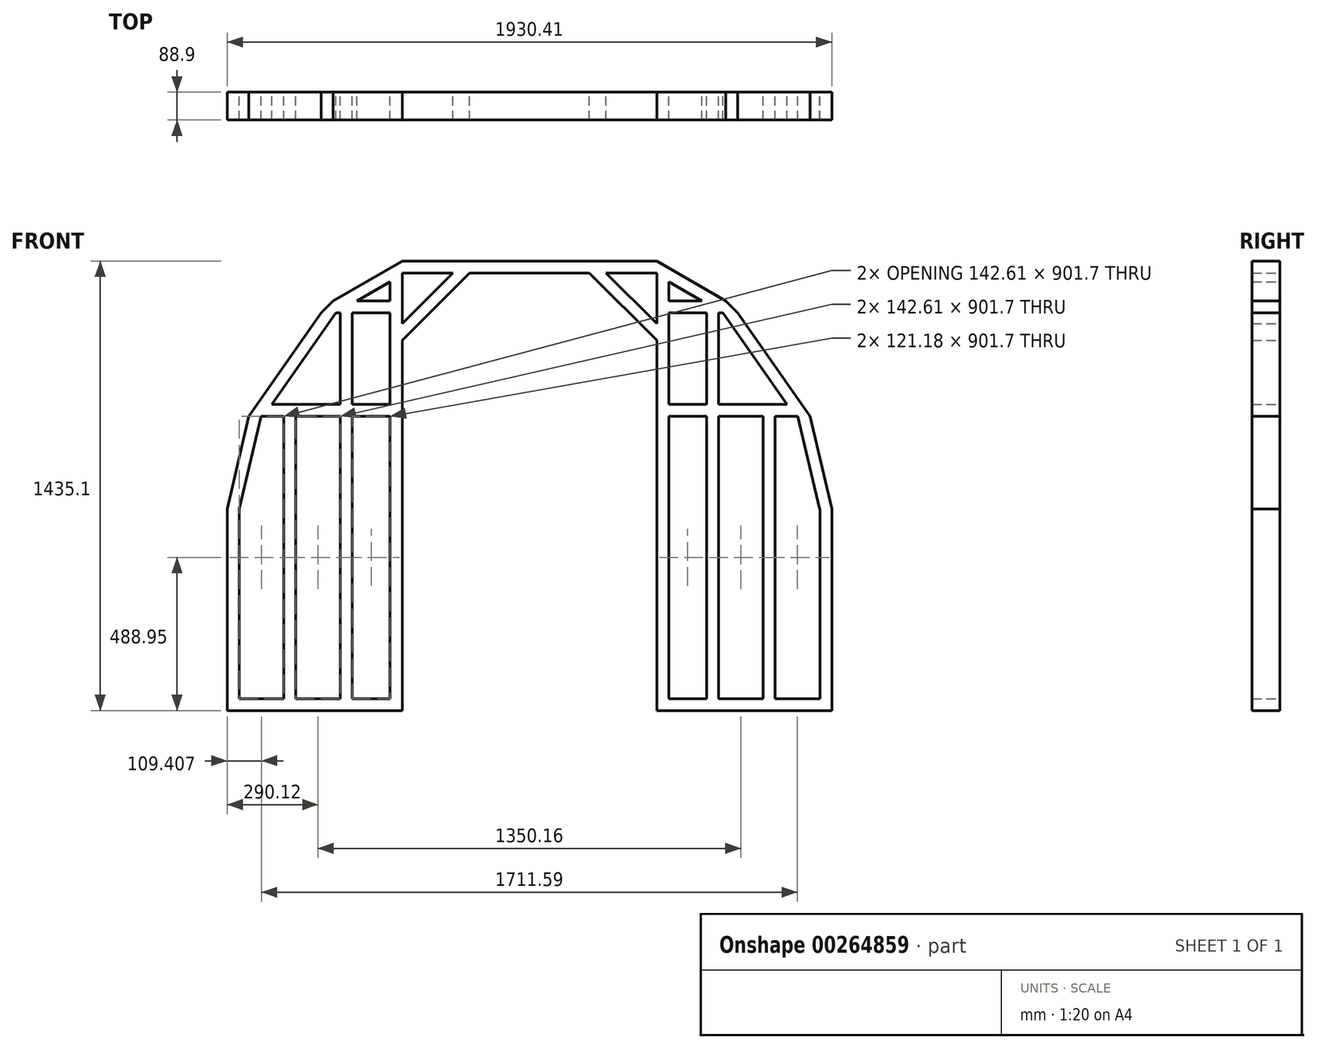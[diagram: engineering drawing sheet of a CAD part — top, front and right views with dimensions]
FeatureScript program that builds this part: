
annotation { "Feature Type Name" : "Feature", "Feature Type Description" : "" }
export const myFeature = defineFeature(function(context is Context, id is Id, definition is map)
    precondition{}
    {
        {
            var Q0;
            Q0=qCreatedBy(makeId("Front.planeOp"),FACE);
            var sketch = newSketch(context, id + "F0", { "sketchPlane" : qUnion([Q0])});
            skLineSegment(sketch, "E0.bottom", {"start": v(0, 0) * mm, "end": v(558.8, 0) * mm});
            skLineSegment(sketch, "E0.top", {"start": v(0, 38.1) * mm, "end": v(218.81, 38.1) * mm});
            skLineSegment(sketch, "E0.right", {"start": v(558.8, 0) * mm, "end": v(558.8, 38.1) * mm});
            skLineSegment(sketch, "E1.bottom", {"start": v(69.52, 939.8) * mm, "end": v(361.43, 939.8) * mm});
            skLineSegment(sketch, "E1.top", {"start": v(96.2, 977.9) * mm, "end": v(361.43, 977.9) * mm});
            skLineSegment(sketch, "E1.right", {"start": v(558.8, 939.8) * mm, "end": v(558.8, 977.9) * mm});
            skLineSegment(sketch, "E2.right", {"start": v(520.7, 1369.1) * mm, "end": v(520.7, 1308.1) * mm});
            skLineSegment(sketch, "E3.1.0.0", {"start": v(361.43, 1270) * mm, "end": v(361.43, 939.8) * mm});
            skLineSegment(sketch, "E3.1.0.1", {"start": v(399.53, 1270) * mm, "end": v(399.53, 38.1) * mm});
            skLineSegment(sketch, "E3.2.0.0", {"start": v(180.71, 939.8) * mm, "end": v(180.71, 38.1) * mm});
            skLineSegment(sketch, "E3.2.0.1", {"start": v(218.81, 939.8) * mm, "end": v(218.81, 38.1) * mm});
            skPoint(sketch, "E4.orphan", {"position": v(0, 939.8) * mm});
            skLineSegment(sketch, "E5.trimOffspring", {"start": v(399.53, 38.1) * mm, "end": v(558.8, 38.1) * mm});
            skLineSegment(sketch, "E6.trimOffspring", {"start": v(218.81, 38.1) * mm, "end": v(399.53, 38.1) * mm});
            skLineSegment(sketch, "E7.bottom", {"start": v(399.53, 939.8) * mm, "end": v(520.7, 939.8) * mm});
            skLineSegment(sketch, "E7.top", {"start": v(338.83, 1308.1) * mm, "end": v(520.7, 1308.1) * mm});
            skLineSegment(sketch, "E7.right", {"start": v(558.8, 38.1) * mm, "end": v(558.8, 1308.1) * mm});
            skLineSegment(sketch, "E8.bottom", {"start": v(558.8, 1308.1) * mm, "end": v(339.99, 1308.1) * mm});
            skLineSegment(sketch, "E8.top", {"start": v(558.8, 1270) * mm, "end": v(361.43, 1270) * mm});
            skLineSegment(sketch, "E8.left", {"start": v(558.8, 1308.1) * mm, "end": v(558.8, 1270) * mm});
            skLineSegment(sketch, "E9", {"start": v(361.43, 1270) * mm, "end": v(300.73, 1270) * mm});
            skLineSegment(sketch, "E10", {"start": v(338.83, 1308.1) * mm, "end": v(300.73, 1270) * mm});
            skLineSegment(sketch, "E11", {"start": v(300.73, 1270) * mm, "end": v(96.2, 977.9) * mm});
            skLineSegment(sketch, "E12", {"start": v(347.24, 1270) * mm, "end": v(142.71, 977.9) * mm});
            skLineSegment(sketch, "E13", {"start": v(338.83, 1308.1) * mm, "end": v(558.8, 1435.1) * mm});
            skLineSegment(sketch, "E14", {"start": v(558.8, 1391.1) * mm, "end": v(415.03, 1308.1) * mm});
            skLineSegment(sketch, "E15.trimOffspring", {"start": v(520.7, 1270) * mm, "end": v(520.7, 38.1) * mm});
            skLineSegment(sketch, "E16.trimOffspring", {"start": v(361.43, 939.8) * mm, "end": v(361.43, 38.1) * mm});
            skLineSegment(sketch, "E17.trimOffspring", {"start": v(399.53, 977.9) * mm, "end": v(520.7, 977.9) * mm});
            skLineSegment(sketch, "E18.trimOffspring", {"start": v(558.8, 939.8) * mm, "end": v(558.8, 939.8) * mm});
            skLineSegment(sketch, "E19.bottom", {"start": v(558.8, 1435.1) * mm, "end": v(965.2, 1435.1) * mm});
            skLineSegment(sketch, "E19.top", {"start": v(558.8, 1397) * mm, "end": v(965.2, 1397) * mm});
            skLineSegment(sketch, "E19.left", {"start": v(558.8, 1435.1) * mm, "end": v(558.8, 1391.1) * mm});
            skLineSegment(sketch, "E20", {"start": v(720.45, 1397) * mm, "end": v(558.8, 1235.36) * mm});
            skLineSegment(sketch, "E21", {"start": v(774.33, 1397) * mm, "end": v(558.8, 1181.47) * mm});
            skLineSegment(sketch, "E22", {"start": v(0, 38.1) * mm, "end": v(0, 643.52) * mm});
            skLineSegment(sketch, "E23", {"start": v(38.1, 38.1) * mm, "end": v(38.1, 643.52) * mm});
            skLineSegment(sketch, "E24", {"start": v(0, 643.52) * mm, "end": v(39.13, 643.52) * mm});
            skLineSegment(sketch, "E25", {"start": v(96.2, 977.9) * mm, "end": v(69.52, 939.8) * mm});
            skLineSegment(sketch, "E26", {"start": v(69.52, 939.8) * mm, "end": v(0, 643.52) * mm});
            skLineSegment(sketch, "E27", {"start": v(39.13, 643.52) * mm, "end": v(108.66, 939.8) * mm});
            skLineSegment(sketch, "E28", {"start": v(0, 38.1) * mm, "end": v(0, 0) * mm});
            skLineSegment(sketch, "E29", {"start": v(558.8, 1391.1) * mm, "end": v(558.8, 1308.1) * mm});
            skLineSegment(sketch, "E30", {"start": v(965.2, 1435.1) * mm, "end": v(965.2, 1397) * mm});
            skSolve(sketch);
        }
        {
            var Q0;
            {var subQ1=sQuery(id+"F0.wireOp",EDGE,"E1.bottom");var subQ5=makeQuery(id+"F0.imprint","INTERSECT",VERTEX,{"derivedFrom":[subQ1,sQuery(id+"F0.wireOp",EDGE,"o7drGsRX-ysO2-n686-hrfP-hiqXFchKHLRx")]});Q0=makeQuery(id+"F0.imprint","IMPRINT",FACE,{"disambiguationData":[TD([[makeQuery(id+"F0.imprint","IMPRINT",EDGE,{"disambiguationData":[TD([[subQ5,1.0]])],"derivedFrom":subQ1}),1.0]])]});}
            var Q1;
            {var subQ6=sQuery(id+"F0.wireOp",EDGE,"E7.top");Q1=makeQuery(id+"F0.imprint","IMPRINT",FACE,{"disambiguationData":[TD([[makeQuery(id+"F0.imprint","IMPRINT",EDGE,{"derivedFrom":subQ6}),-1.0]])]});}
            var Q2;
            {var subQ2=sQuery(id+"F0.wireOp",EDGE,"E7.top");Q2=makeQuery(id+"F0.imprint","IMPRINT",FACE,{"disambiguationData":[TD([[makeQuery(id+"F0.imprint","IMPRINT",EDGE,{"derivedFrom":subQ2}),1.0]])]});}
            var Q3;
            {var subQ0=sQuery(id+"F0.wireOp",EDGE,"E2.right");Q3=makeQuery(id+"F0.imprint","IMPRINT",FACE,{"disambiguationData":[TD([[makeQuery(id+"F0.imprint","IMPRINT",EDGE,{"derivedFrom":subQ0}),1.0]])]});}
            var Q4;
            {var subQ5=sQuery(id+"F0.wireOp",EDGE,"E16.trimOffspring");Q4=makeQuery(id+"F0.imprint","IMPRINT",FACE,{"disambiguationData":[TD([[makeQuery(id+"F0.imprint","IMPRINT",EDGE,{"derivedFrom":subQ5}),1.0]])]});}
            var Q5;
            {var subQ0=sQuery(id+"F0.wireOp",EDGE,"E8.top");var subQ3=sQuery(id+"F0.wireOp",EDGE,"E12");var subQ5=makeQuery(id+"F0.imprint","INTERSECT",VERTEX,{"derivedFrom":[subQ0,subQ3]});Q5=makeQuery(id+"F0.imprint","IMPRINT",FACE,{"disambiguationData":[TD([[makeQuery(id+"F0.imprint","IMPRINT",EDGE,{"disambiguationData":[TD([[subQ5,-1.0]])],"derivedFrom":subQ3}),-1.0]])]});}
            var Q6;
            {var subQ2=sQuery(id+"F0.wireOp",EDGE,"f34f2ac7-a2c3-40e4-8003-bd70d18b0446.right");var subQ8=makeQuery(id+"F0.imprint","IMPRINT",VERTEX,{"derivedFrom":subQ2});Q6=makeQuery(id+"F0.imprint","IMPRINT",FACE,{"disambiguationData":[TD([[makeQuery(id+"F0.imprint","IMPRINT",EDGE,{"disambiguationData":[TD([[subQ8,1.0]])],"derivedFrom":subQ2}),1.0]])]});}
            var Q7;
            {var subQ0=sQuery(id+"F0.wireOp",EDGE,"E17.trimOffspring");Q7=makeQuery(id+"F0.imprint","IMPRINT",FACE,{"disambiguationData":[TD([[makeQuery(id+"F0.imprint","IMPRINT",EDGE,{"derivedFrom":subQ0}),-1.0]])]});}
            var Q8;
            {var subQ7=sQuery(id+"F0.wireOp",EDGE,"E0.bottom");Q8=makeQuery(id+"F0.imprint","IMPRINT",FACE,{"disambiguationData":[TD([[makeQuery(id+"F0.imprint","IMPRINT",EDGE,{"derivedFrom":subQ7}),1.0]])]});}
            var Q9;
            {var subQ0=sQuery(id+"F0.wireOp",EDGE,"E3.3.0.0");Q9=makeQuery(id+"F0.imprint","IMPRINT",FACE,{"disambiguationData":[TD([[makeQuery(id+"F0.imprint","IMPRINT",EDGE,{"derivedFrom":subQ0}),1.0]])]});}
            var Q10;
            {var subQ1=sQuery(id+"F0.wireOp",EDGE,"UqQhR3tJ-lLPc-B1ja-KThw-if7eZAOedKC9");Q10=makeQuery(id+"F0.imprint","IMPRINT",FACE,{"disambiguationData":[TD([[makeQuery(id+"F0.imprint","IMPRINT",EDGE,{"derivedFrom":subQ1}),1.0]])]});}
            var Q11;
            {var subQ3=sQuery(id+"F0.wireOp",EDGE,"E3.2.0.0");Q11=makeQuery(id+"F0.imprint","IMPRINT",FACE,{"disambiguationData":[TD([[makeQuery(id+"F0.imprint","IMPRINT",EDGE,{"derivedFrom":subQ3}),1.0]])]});}
            var Q12;
            {var subQ0=sQuery(id+"F0.wireOp",EDGE,"a6b2e4c6-b9f2-484d-9ff3-2c9e5a26dfd725.MirrorCS");Q12=makeQuery(id+"F0.imprint","IMPRINT",FACE,{"disambiguationData":[TD([[makeQuery(id+"F0.imprint","IMPRINT",EDGE,{"derivedFrom":subQ0}),1.0]])]});}
            var Q13;
            {var subQ0=sQuery(id+"F0.wireOp",EDGE,"a6b2e4c6-b9f2-484d-9ff3-2c9e5a26dfd715.MirrorCS");Q13=makeQuery(id+"F0.imprint","IMPRINT",FACE,{"disambiguationData":[TD([[makeQuery(id+"F0.imprint","IMPRINT",EDGE,{"derivedFrom":subQ0}),1.0]])]});}
            var Q14;
            {var subQ5=sQuery(id+"F0.wireOp",EDGE,"a6b2e4c6-b9f2-484d-9ff3-2c9e5a26dfd75.MirrorCS");Q14=makeQuery(id+"F0.imprint","IMPRINT",FACE,{"disambiguationData":[TD([[makeQuery(id+"F0.imprint","IMPRINT",EDGE,{"derivedFrom":subQ5}),1.0]])]});}
            var Q15;
            {var subQ5=sQuery(id+"F0.wireOp",EDGE,"a6b2e4c6-b9f2-484d-9ff3-2c9e5a26dfd77.MirrorCS");Q15=makeQuery(id+"F0.imprint","IMPRINT",FACE,{"disambiguationData":[TD([[makeQuery(id+"F0.imprint","IMPRINT",EDGE,{"derivedFrom":subQ5}),-1.0]])]});}
            var Q16;
            {var subQ0=sQuery(id+"F0.wireOp",EDGE,"a6b2e4c6-b9f2-484d-9ff3-2c9e5a26dfd724.MirrorCS");var subQ2=sQuery(id+"F0.wireOp",EDGE,"8b6cf107-65ec-4715-8105-ea0a48015bdc.trimOffspring");var subQ3=makeQuery(id+"F0.imprint","INTERSECT",VERTEX,{"derivedFrom":[subQ2,subQ0]});Q16=makeQuery(id+"F0.imprint","IMPRINT",FACE,{"disambiguationData":[TD([[makeQuery(id+"F0.imprint","IMPRINT",EDGE,{"disambiguationData":[TD([[subQ3,-1.0]])],"derivedFrom":subQ2}),1.0]])]});}
            var Q17;
            {var subQ6=sQuery(id+"F0.wireOp",EDGE,"a6b2e4c6-b9f2-484d-9ff3-2c9e5a26dfd75.MirrorCS");Q17=makeQuery(id+"F0.imprint","IMPRINT",FACE,{"disambiguationData":[TD([[makeQuery(id+"F0.imprint","IMPRINT",EDGE,{"derivedFrom":subQ6}),-1.0]])]});}
            var Q18;
            {var subQ0=sQuery(id+"F0.wireOp",EDGE,"a6b2e4c6-b9f2-484d-9ff3-2c9e5a26dfd729.MirrorCS");var subQ3=makeQuery(id+"F0.imprint","INTERSECT",VERTEX,{"derivedFrom":[subQ0,sQuery(id+"F0.wireOp",EDGE,"a6b2e4c6-b9f2-484d-9ff3-2c9e5a26dfd739.MirrorCS")]});Q18=makeQuery(id+"F0.imprint","IMPRINT",FACE,{"disambiguationData":[TD([[makeQuery(id+"F0.imprint","IMPRINT",EDGE,{"disambiguationData":[TD([[subQ3,1.0]])],"derivedFrom":subQ0}),-1.0]])]});}
            var Q19;
            {var subQ0=sQuery(id+"F0.wireOp",EDGE,"a6b2e4c6-b9f2-484d-9ff3-2c9e5a26dfd722.MirrorCS");Q19=makeQuery(id+"F0.imprint","IMPRINT",FACE,{"disambiguationData":[TD([[makeQuery(id+"F0.imprint","IMPRINT",EDGE,{"derivedFrom":subQ0}),-1.0]])]});}
            var Q20;
            {var subQ0=sQuery(id+"F0.wireOp",EDGE,"a6b2e4c6-b9f2-484d-9ff3-2c9e5a26dfd720.MirrorCS");var subQ1=sQuery(id+"F0.wireOp",EDGE,"8b6cf107-65ec-4715-8105-ea0a48015bdc.trimOffspring");var subQ2=makeQuery(id+"F0.imprint","INTERSECT",VERTEX,{"derivedFrom":[subQ1,subQ0]});Q20=makeQuery(id+"F0.imprint","IMPRINT",FACE,{"disambiguationData":[TD([[makeQuery(id+"F0.imprint","IMPRINT",EDGE,{"disambiguationData":[TD([[subQ2,-1.0]])],"derivedFrom":subQ1}),1.0]])]});}
            var Q21;
            {var subQ0=sQuery(id+"F0.wireOp",EDGE,"a6b2e4c6-b9f2-484d-9ff3-2c9e5a26dfd739.MirrorCS");Q21=makeQuery(id+"F0.imprint","IMPRINT",FACE,{"disambiguationData":[TD([[makeQuery(id+"F0.imprint","IMPRINT",EDGE,{"derivedFrom":subQ0}),1.0]])]});}
            var Q22;
            {var subQ0=sQuery(id+"F0.wireOp",EDGE,"a6b2e4c6-b9f2-484d-9ff3-2c9e5a26dfd728.MirrorCS");Q22=makeQuery(id+"F0.imprint","IMPRINT",FACE,{"disambiguationData":[TD([[makeQuery(id+"F0.imprint","IMPRINT",EDGE,{"derivedFrom":subQ0}),-1.0]])]});}
            var Q23;
            {var subQ8=sQuery(id+"F0.wireOp",EDGE,"a6b2e4c6-b9f2-484d-9ff3-2c9e5a26dfd712.MirrorCS");Q23=makeQuery(id+"F0.imprint","IMPRINT",FACE,{"disambiguationData":[TD([[makeQuery(id+"F0.imprint","IMPRINT",EDGE,{"derivedFrom":subQ8}),-1.0]])]});}
            var Q24;
            {var subQ0=sQuery(id+"F0.wireOp",EDGE,"E5.trimOffspring");var subQ2=sQuery(id+"F0.wireOp",EDGE,"f34f2ac7-a2c3-40e4-8003-bd70d18b0446.right");var subQ3=makeQuery(id+"F0.imprint","INTERSECT",VERTEX,{"derivedFrom":[subQ2,subQ0]});Q24=makeQuery(id+"F0.imprint","IMPRINT",FACE,{"disambiguationData":[TD([[makeQuery(id+"F0.imprint","IMPRINT",EDGE,{"disambiguationData":[TD([[subQ3,-1.0]])],"derivedFrom":subQ2}),1.0]])]});}
            var Q25;
            {var subQ6=sQuery(id+"F0.wireOp",EDGE,"a6b2e4c6-b9f2-484d-9ff3-2c9e5a26dfd720.MirrorCS");var subQ8=makeQuery(id+"F0.imprint","INTERSECT",VERTEX,{"derivedFrom":[subQ6,sQuery(id+"F0.wireOp",EDGE,"36c52472-8055-443f-a80e-24cd42e96d6a.trimOffspring")]});Q25=makeQuery(id+"F0.imprint","IMPRINT",FACE,{"disambiguationData":[TD([[makeQuery(id+"F0.imprint","IMPRINT",EDGE,{"disambiguationData":[TD([[subQ8,1.0]])],"derivedFrom":subQ6}),1.0]])]});}
            var Q26;
            {var subQ7=sQuery(id+"F0.wireOp",EDGE,"a6b2e4c6-b9f2-484d-9ff3-2c9e5a26dfd726.MirrorCS");var subQ8=sQuery(id+"F0.wireOp",EDGE,"a6b2e4c6-b9f2-484d-9ff3-2c9e5a26dfd724.MirrorCS");var subQ9=makeQuery(id+"F0.imprint","INTERSECT",VERTEX,{"derivedFrom":[subQ8,subQ7]});Q26=makeQuery(id+"F0.imprint","IMPRINT",FACE,{"disambiguationData":[TD([[makeQuery(id+"F0.imprint","IMPRINT",EDGE,{"disambiguationData":[TD([[subQ9,-1.0]])],"derivedFrom":subQ8}),1.0]])]});}
            var Q27;
            {var subQ1=sQuery(id+"F0.wireOp",EDGE,"a6b2e4c6-b9f2-484d-9ff3-2c9e5a26dfd726.MirrorCS");var subQ3=sQuery(id+"F0.wireOp",EDGE,"a6b2e4c6-b9f2-484d-9ff3-2c9e5a26dfd740.MirrorCS");var subQ4=makeQuery(id+"F0.imprint","INTERSECT",VERTEX,{"derivedFrom":[subQ1,subQ3]});Q27=makeQuery(id+"F0.imprint","IMPRINT",FACE,{"disambiguationData":[TD([[makeQuery(id+"F0.imprint","IMPRINT",EDGE,{"disambiguationData":[TD([[subQ4,-1.0]])],"derivedFrom":subQ3}),1.0]])]});}
            var Q28;
            {var subQ3=sQuery(id+"F0.wireOp",EDGE,"ad4d54da-d475-416e-85dd-e6266885aeb10.MirrorCS");var subQ5=makeQuery(id+"F0.imprint","IMPRINT",VERTEX,{"derivedFrom":subQ3});Q28=makeQuery(id+"F0.imprint","IMPRINT",FACE,{"disambiguationData":[TD([[makeQuery(id+"F0.imprint","IMPRINT",EDGE,{"disambiguationData":[TD([[subQ5,1.0]])],"derivedFrom":subQ3}),-1.0]])]});}
            var Q29;
            {var subQ0=sQuery(id+"F0.wireOp",EDGE,"E20");Q29=makeQuery(id+"F0.imprint","IMPRINT",FACE,{"disambiguationData":[TD([[makeQuery(id+"F0.imprint","IMPRINT",EDGE,{"derivedFrom":subQ0}),1.0]])]});}
            var Q30;
            {var subQ0=sQuery(id+"F0.wireOp",EDGE,"ea44d06e-db00-4769-aa4d-0e3a6f6b15990.MirrorCS");Q30=makeQuery(id+"F0.imprint","IMPRINT",FACE,{"disambiguationData":[TD([[makeQuery(id+"F0.imprint","IMPRINT",EDGE,{"derivedFrom":subQ0}),1.0]])]});}
            var Q31;
            {var subQ1=sQuery(id+"F0.wireOp",EDGE,"E22");Q31=makeQuery(id+"F0.imprint","IMPRINT",FACE,{"disambiguationData":[TD([[makeQuery(id+"F0.imprint","IMPRINT",EDGE,{"derivedFrom":subQ1}),-1.0]])]});}
            var Q32;
            {var subQ0=sQuery(id+"F0.wireOp",EDGE,"E11");Q32=makeQuery(id+"F0.imprint","IMPRINT",FACE,{"disambiguationData":[TD([[makeQuery(id+"F0.imprint","IMPRINT",EDGE,{"derivedFrom":subQ0}),1.0]])]});}
            var Q33;
            {var subQ0=sQuery(id+"F0.wireOp",EDGE,"E26");Q33=makeQuery(id+"F0.imprint","IMPRINT",FACE,{"disambiguationData":[TD([[makeQuery(id+"F0.imprint","IMPRINT",EDGE,{"derivedFrom":subQ0}),1.0]])]});}
            var Q34;
            {var subQ5=sQuery(id+"F0.wireOp",EDGE,"E7.right");var subQ9=makeQuery(id+"F0.imprint","IMPRINT",VERTEX,{"disambiguationData":[OD(0.0)],"derivedFrom":subQ5});Q34=makeQuery(id+"F0.imprint","IMPRINT",FACE,{"disambiguationData":[TD([[makeQuery(id+"F0.imprint","IMPRINT",EDGE,{"disambiguationData":[TD([[subQ9,1.0]])],"derivedFrom":subQ5}),1.0]])]});}
            var Q35;
            {var subQ6=sQuery(id+"F0.wireOp",EDGE,"E19.bottom");Q35=makeQuery(id+"F0.imprint","IMPRINT",FACE,{"disambiguationData":[TD([[makeQuery(id+"F0.imprint","IMPRINT",EDGE,{"derivedFrom":subQ6}),-1.0]])]});}
            extrude(context, id + "F1", {"entities" : qUnion([Q0, Q1, Q2, Q3, Q4, Q5, Q6, Q7, Q8, Q9, Q10, Q11, Q12, Q13, Q14, Q15, Q16, Q17, Q18, Q19, Q20, Q21, Q22, Q23, Q24, Q25, Q26, Q27, Q28, Q29, Q30, Q31, Q32, Q33, Q34, Q35]), "depth" : 88.9 * mm, "offsetDistance" : 25.4 * mm});
        }
        {
            var Q0;
            Q0=makeQuery(id+"F1.opExtrude","SWEPT_BODY",BODY,{"disambiguationData":[OSD([sQuery(id+"F0.wireOp",EDGE,"E0.top"),sQuery(id+"F0.wireOp",EDGE,"E1.bottom"),sQuery(id+"F0.wireOp",EDGE,"E1.top"),sQuery(id+"F0.wireOp",EDGE,"E2.right"),sQuery(id+"F0.wireOp",EDGE,"f34f2ac7-a2c3-40e4-8003-bd70d18b0446.right"),sQuery(id+"F0.wireOp",EDGE,"E3.1.0.0"),sQuery(id+"F0.wireOp",EDGE,"E3.1.0.1"),sQuery(id+"F0.wireOp",EDGE,"E3.2.0.0"),sQuery(id+"F0.wireOp",EDGE,"E3.2.0.1"),sQuery(id+"F0.wireOp",EDGE,"E5.trimOffspring"),sQuery(id+"F0.wireOp",EDGE,"E6.trimOffspring"),sQuery(id+"F0.wireOp",EDGE,"E7.right"),sQuery(id+"F0.wireOp",EDGE,"E8.bottom"),sQuery(id+"F0.wireOp",EDGE,"E8.top"),sQuery(id+"F0.wireOp",EDGE,"E8.left"),sQuery(id+"F0.wireOp",EDGE,"E10"),sQuery(id+"F0.wireOp",EDGE,"E11"),sQuery(id+"F0.wireOp",EDGE,"E12"),sQuery(id+"F0.wireOp",EDGE,"E13"),sQuery(id+"F0.wireOp",EDGE,"E14"),sQuery(id+"F0.wireOp",EDGE,"E15.trimOffspring"),sQuery(id+"F0.wireOp",EDGE,"E16.trimOffspring"),sQuery(id+"F0.wireOp",EDGE,"E17.trimOffspring"),sQuery(id+"F0.wireOp",EDGE,"E7.bottom"),sQuery(id+"F0.wireOp",EDGE,"E19.bottom"),sQuery(id+"F0.wireOp",EDGE,"E19.top"),sQuery(id+"F0.wireOp",EDGE,"E20"),sQuery(id+"F0.wireOp",EDGE,"E21"),sQuery(id+"F0.wireOp",EDGE,"E22"),sQuery(id+"F0.wireOp",EDGE,"E23"),sQuery(id+"F0.wireOp",EDGE,"E24"),sQuery(id+"F0.wireOp",EDGE,"Sjl2GybE-2uOU-1785-080H-XiCMymYNMAR1"),sQuery(id+"F0.wireOp",EDGE,"E25"),sQuery(id+"F0.wireOp",EDGE,"E26"),sQuery(id+"F0.wireOp",EDGE,"E27")])]});
            var Q1;
            Q1=makeQuery(id+"F1.opExtrude","SWEPT_FACE",FACE,{"disambiguationData":[OSD([sQuery(id+"F0.wireOp",EDGE,"E30")])]});
            mirror(context, id + "F2", {"operationType" : NewBodyOperationType.ADD, "entities" : qUnion([Q0]), "mirrorPlane" : qUnion([Q1])});
        }
    });
